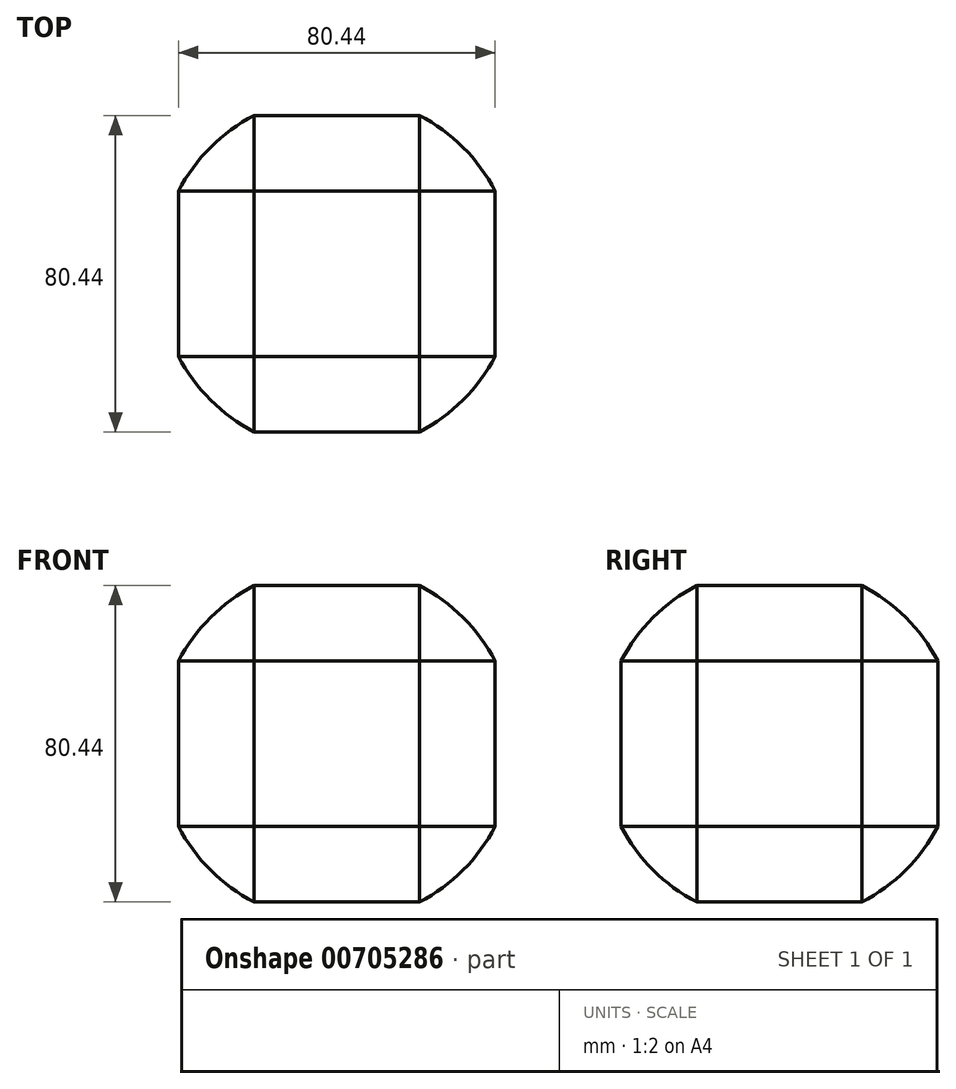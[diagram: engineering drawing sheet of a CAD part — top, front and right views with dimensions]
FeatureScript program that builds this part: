
annotation { "Feature Type Name" : "Feature", "Feature Type Description" : "" }
export const myFeature = defineFeature(function(context is Context, id is Id, definition is map)
    precondition{}
    {
        {
            var Q0;
            Q0=qCreatedBy(makeId("Top.planeOp"),FACE);
            var sketch = newSketch(context, id + "F0", { "sketchPlane" : qUnion([Q0])});
            skCircle(sketch, "E0", {"center": v(0, 0) * mm, "radius": 50 * mm});
            skLineSegment(sketch, "E1", {"start": v(0, 0) * mm, "end": v(69.26, 0) * mm, "construction": true});
            skLineSegment(sketch, "E2", {"start": v(0, 0) * mm, "end": v(-59.91, 0) * mm});
            skLineSegment(sketch, "E3", {"start": v(-59.91, 0) * mm, "end": v(73.8, 0) * mm});
            skSolve(sketch);
        }
        {
            var Q0;
            {var subQ0=sQuery(id+"F0.wireOp",EDGE,"E2");var subQ1=sQuery(id+"F0.wireOp",EDGE,"E0");var subQ2=makeQuery(id+"F0.imprint","INTERSECT",VERTEX,{"derivedFrom":[subQ1,subQ0]});Q0=makeQuery(id+"F0.imprint","IMPRINT",FACE,{"disambiguationData":[TD([[makeQuery(id+"F0.imprint","IMPRINT",EDGE,{"disambiguationData":[TD([[subQ2,1.0]])],"derivedFrom":subQ1}),1.0]])]});}
            var Q1;
            Q1=sQuery(id+"F0.wireOp",EDGE,"E3");
            revolve(context, id + "F1", {"surfaceOperationType" : NewSurfaceOperationType.NEW, "entities" : qUnion([Q0]), "axis" : qUnion([Q1]), "revolveType" : RevolveType.FULL});
        }
        {
            var Q0;
            Q0=qCreatedBy(makeId("Top.planeOp"),FACE);
            cPlane(context, id + "F2", {"entities" : qUnion([Q0]), "cplaneType" : CPlaneType.OFFSET, "offset" : 60 * mm, "width" : 150 * mm, "height" : 150 * mm});
        }
        {
            var Q0;
            Q0=qCreatedBy(id+"F2.planeOp",FACE);
            var sketch = newSketch(context, id + "F3", { "sketchPlane" : qUnion([Q0])});
            skCircle(sketch, "E4", {"center": v(0, 0) * mm, "radius": 45.37 * mm});
            skCircle(sketch, "E5", {"center": v(0, 0) * mm, "radius": 120.1 * mm});
            skSolve(sketch);
        }
        {
            var Q0;
            Q0=makeQuery(id+"F3.imprint","IMPRINT",FACE,{"disambiguationData":[TD([[makeQuery(id+"F3.imprint","IMPRINT",EDGE,{"derivedFrom":sQuery(id+"F3.wireOp",EDGE,"E4")}),-1.0]])]});
            extrude(context, id + "F4", {"entities" : qUnion([Q0]), "operationType" : NewBodyOperationType.REMOVE, "endBound" : BoundingType.THROUGH_ALL, "oppositeDirection" : true, "depth" : 25 * mm, "offsetDistance" : 25 * mm});
        }
        {
            var Q0;
            Q0=qCreatedBy(makeId("Front.planeOp"),FACE);
            cPlane(context, id + "F5", {"entities" : qUnion([Q0]), "cplaneType" : CPlaneType.OFFSET, "offset" : 60 * mm, "width" : 150 * mm, "height" : 150 * mm});
        }
        {
            var Q0;
            Q0=qCreatedBy(makeId("Right.planeOp"),FACE);
            cPlane(context, id + "F6", {"entities" : qUnion([Q0]), "cplaneType" : CPlaneType.OFFSET, "offset" : 60 * mm, "width" : 150 * mm, "height" : 150 * mm});
        }
        {
            var Q0;
            Q0=qCreatedBy(id+"F5.planeOp",FACE);
            var sketch = newSketch(context, id + "F7", { "sketchPlane" : qUnion([Q0])});
            skCircle(sketch, "E6", {"center": v(0, 0) * mm, "radius": 45.38 * mm});
            skCircle(sketch, "E7", {"center": v(0, 0) * mm, "radius": 63.17 * mm});
            skSolve(sketch);
        }
        {
            var Q0;
            Q0=makeQuery(id+"F7.imprint","IMPRINT",FACE,{"disambiguationData":[TD([[makeQuery(id+"F7.imprint","IMPRINT",EDGE,{"derivedFrom":sQuery(id+"F7.wireOp",EDGE,"E6")}),-1.0]])]});
            extrude(context, id + "F8", {"entities" : qUnion([Q0]), "operationType" : NewBodyOperationType.REMOVE, "endBound" : BoundingType.THROUGH_ALL, "oppositeDirection" : true, "depth" : 25 * mm, "offsetDistance" : 25 * mm});
        }
        {
            var Q0;
            Q0=qCreatedBy(id+"F6.planeOp",FACE);
            var sketch = newSketch(context, id + "F9", { "sketchPlane" : qUnion([Q0])});
            skCircle(sketch, "E8", {"center": v(0, 0) * mm, "radius": 45.38 * mm});
            skCircle(sketch, "E9", {"center": v(0, 0) * mm, "radius": 73.07 * mm});
            skSolve(sketch);
        }
        {
            var Q0;
            Q0=makeQuery(id+"F9.imprint","IMPRINT",FACE,{"disambiguationData":[TD([[makeQuery(id+"F9.imprint","IMPRINT",EDGE,{"derivedFrom":sQuery(id+"F9.wireOp",EDGE,"E8")}),-1.0]])]});
            extrude(context, id + "F10", {"entities" : qUnion([Q0]), "operationType" : NewBodyOperationType.REMOVE, "endBound" : BoundingType.THROUGH_ALL, "oppositeDirection" : true, "depth" : 25 * mm, "offsetDistance" : 25 * mm});
        }
        {
            var Q0;
            Q0=qCreatedBy(makeId("Right.planeOp"),FACE);
            var Q1;
            Q1=makeQuery(id+"F8.boolean.opBoolean","INTERSECT",VERTEX,{"disambiguationData":[OD(2.0)],"derivedFrom":[makeQuery(id+"F4.boolean.opBoolean","COPY",FACE,{"derivedFrom":makeQuery(id+"F4.opExtrude","SWEPT_FACE",FACE,{"disambiguationData":[OSD([sQuery(id+"F3.wireOp",EDGE,"E4")])]})}),makeQuery(id+"F4.boolean.opBoolean","SPLIT",FACE,{"disambiguationData":[OD(0.0)],"derivedFrom":makeQuery(id+"F1.opRevolve","SWEPT_FACE",FACE,{"disambiguationData":[OSD([sQuery(id+"F0.wireOp",EDGE,"E0")])]})}),makeQuery(id+"F8.opExtrude","SWEPT_FACE",FACE,{"disambiguationData":[OSD([sQuery(id+"F7.wireOp",EDGE,"E6")])]})]});
            cPlane(context, id + "F11", {"entities" : qUnion([Q0, Q1]), "cplaneType" : CPlaneType.PLANE_POINT, "offset" : 25 * mm, "width" : 150 * mm, "height" : 150 * mm});
        }
        {
            var Q0;
            Q0=qCreatedBy(id+"F11.planeOp",FACE);
            var sketch = newSketch(context, id + "F12", { "sketchPlane" : qUnion([Q0])});
            skLineSegment(sketch, "E10.bottom", {"start": v(-21, 21) * mm, "end": v(21, 21) * mm});
            skLineSegment(sketch, "E10.top", {"start": v(-21, -21) * mm, "end": v(21, -21) * mm});
            skLineSegment(sketch, "E10.left", {"start": v(-21, 21) * mm, "end": v(-21, -21) * mm});
            skLineSegment(sketch, "E10.right", {"start": v(21, 21) * mm, "end": v(21, -21) * mm});
            skSolve(sketch);
        }
        {
            var Q0;
            Q0=makeQuery(id+"F12.imprint","IMPRINT",FACE,{"disambiguationData":[TD([[makeQuery(id+"F12.imprint","IMPRINT",EDGE,{"derivedFrom":sQuery(id+"F12.wireOp",EDGE,"E10.bottom")}),-1.0]])]});
            extrude(context, id + "F13", {"entities" : qUnion([Q0]), "operationType" : NewBodyOperationType.REMOVE, "endBound" : BoundingType.THROUGH_ALL, "depth" : 25 * mm, "offsetDistance" : 25 * mm});
        }
        {
            var Q0;
            Q0=qCreatedBy(makeId("Right.planeOp"),FACE);
            var Q1;
            Q1=makeQuery(id+"F8.boolean.opBoolean","INTERSECT",VERTEX,{"disambiguationData":[OD(1.0)],"derivedFrom":[makeQuery(id+"F4.boolean.opBoolean","COPY",FACE,{"derivedFrom":makeQuery(id+"F4.opExtrude","SWEPT_FACE",FACE,{"disambiguationData":[OSD([sQuery(id+"F3.wireOp",EDGE,"E4")])]})}),makeQuery(id+"F4.boolean.opBoolean","SPLIT",FACE,{"disambiguationData":[OD(1.0)],"derivedFrom":makeQuery(id+"F1.opRevolve","SWEPT_FACE",FACE,{"disambiguationData":[OSD([sQuery(id+"F0.wireOp",EDGE,"E0")])]})}),makeQuery(id+"F8.opExtrude","SWEPT_FACE",FACE,{"disambiguationData":[OSD([sQuery(id+"F7.wireOp",EDGE,"E6")])]})]});
            cPlane(context, id + "F14", {"entities" : qUnion([Q0, Q1]), "cplaneType" : CPlaneType.PLANE_POINT, "offset" : 25 * mm, "width" : 150 * mm, "height" : 150 * mm});
        }
        {
            var Q0;
            Q0=qCreatedBy(id+"F14.planeOp",FACE);
            var sketch = newSketch(context, id + "F15", { "sketchPlane" : qUnion([Q0])});
            skLineSegment(sketch, "E11.bottom", {"start": v(21, 21) * mm, "end": v(-21, 21) * mm});
            skLineSegment(sketch, "E11.top", {"start": v(21, -21) * mm, "end": v(-21, -21) * mm});
            skLineSegment(sketch, "E11.left", {"start": v(21, 21) * mm, "end": v(21, -21) * mm});
            skLineSegment(sketch, "E11.right", {"start": v(-21, 21) * mm, "end": v(-21, -21) * mm});
            skSolve(sketch);
        }
        {
            var Q0;
            Q0=makeQuery(id+"F15.imprint","IMPRINT",FACE,{"disambiguationData":[TD([[makeQuery(id+"F15.imprint","IMPRINT",EDGE,{"derivedFrom":sQuery(id+"F15.wireOp",EDGE,"E11.bottom")}),1.0]])]});
            extrude(context, id + "F16", {"entities" : qUnion([Q0]), "operationType" : NewBodyOperationType.REMOVE, "endBound" : BoundingType.THROUGH_ALL, "oppositeDirection" : true, "depth" : 25 * mm, "offsetDistance" : 25 * mm});
        }
        {
            var Q0;
            Q0=qCreatedBy(makeId("Top.planeOp"),FACE);
            var Q1;
            Q1=makeQuery(id+"F10.boolean.opBoolean","INTERSECT",VERTEX,{"disambiguationData":[OD(1.0)],"derivedFrom":[makeQuery(id+"F8.boolean.opBoolean","SPLIT",FACE,{"disambiguationData":[OD(1.0)],"derivedFrom":makeQuery(id+"F4.boolean.opBoolean","SPLIT",FACE,{"disambiguationData":[OD(1.0)],"derivedFrom":makeQuery(id+"F1.opRevolve","SWEPT_FACE",FACE,{"disambiguationData":[OSD([sQuery(id+"F0.wireOp",EDGE,"E0")])]})})}),makeQuery(id+"F8.boolean.opBoolean","COPY",FACE,{"disambiguationData":[OD(1.0)],"derivedFrom":makeQuery(id+"F8.opExtrude","SWEPT_FACE",FACE,{"disambiguationData":[OSD([sQuery(id+"F7.wireOp",EDGE,"E6")])]})}),makeQuery(id+"F10.opExtrude","SWEPT_FACE",FACE,{"disambiguationData":[OSD([sQuery(id+"F9.wireOp",EDGE,"E8")])]})]});
            cPlane(context, id + "F17", {"entities" : qUnion([Q0, Q1]), "cplaneType" : CPlaneType.PLANE_POINT, "offset" : 25 * mm, "width" : 150 * mm, "height" : 150 * mm});
        }
        {
            var Q0;
            Q0=qCreatedBy(id+"F17.planeOp",FACE);
            var sketch = newSketch(context, id + "F18", { "sketchPlane" : qUnion([Q0])});
            skLineSegment(sketch, "E12.bottom", {"start": v(-21, 21) * mm, "end": v(21, 21) * mm});
            skLineSegment(sketch, "E12.top", {"start": v(-21, -21) * mm, "end": v(21, -21) * mm});
            skLineSegment(sketch, "E12.left", {"start": v(-21, 21) * mm, "end": v(-21, -21) * mm});
            skLineSegment(sketch, "E12.right", {"start": v(21, 21) * mm, "end": v(21, -21) * mm});
            skSolve(sketch);
        }
        {
            var Q0;
            Q0=makeQuery(id+"F18.imprint","IMPRINT",FACE,{"disambiguationData":[TD([[makeQuery(id+"F18.imprint","IMPRINT",EDGE,{"derivedFrom":sQuery(id+"F18.wireOp",EDGE,"E12.bottom")}),-1.0]])]});
            extrude(context, id + "F19", {"entities" : qUnion([Q0]), "operationType" : NewBodyOperationType.REMOVE, "endBound" : BoundingType.THROUGH_ALL, "depth" : 25 * mm, "offsetDistance" : 25 * mm});
        }
        {
            var Q0;
            Q0=qCreatedBy(makeId("Front.planeOp"),FACE);
            var sketch = newSketch(context, id + "F20", { "sketchPlane" : qUnion([Q0])});
            skLineSegment(sketch, "E13.bottom", {"start": v(21, -58.86) * mm, "end": v(-21, -58.86) * mm});
            skLineSegment(sketch, "E13.top", {"start": v(21, -40.22) * mm, "end": v(-21, -40.22) * mm});
            skLineSegment(sketch, "E13.left", {"start": v(21, -58.86) * mm, "end": v(21, -40.22) * mm});
            skLineSegment(sketch, "E13.right", {"start": v(-21, -58.86) * mm, "end": v(-21, -40.22) * mm});
            skSolve(sketch);
        }
        {
            var Q0;
            Q0 = qSketchRegion(id + "F20", true);
            extrude(context, id + "F21", {"entities" : qUnion([Q0]), "operationType" : NewBodyOperationType.REMOVE, "endBound" : BoundingType.THROUGH_ALL, "oppositeDirection" : true, "depth" : 25 * mm, "offsetDistance" : 25 * mm, "hasSecondDirection" : true, "secondDirectionBound" : SecondDirectionBoundingType.THROUGH_ALL, "secondDirectionOppositeDirection" : false, "secondDirectionDepth" : 25 * mm});
        }
        {
            var Q0;
            Q0=qCreatedBy(makeId("Right.planeOp"),FACE);
            var sketch = newSketch(context, id + "F22", { "sketchPlane" : qUnion([Q0])});
            skLineSegment(sketch, "E14.bottom", {"start": v(-53.94, 21) * mm, "end": v(-40.22, 21) * mm});
            skLineSegment(sketch, "E14.top", {"start": v(-53.94, -21) * mm, "end": v(-40.22, -21) * mm});
            skLineSegment(sketch, "E14.left", {"start": v(-53.94, 21) * mm, "end": v(-53.94, -21) * mm});
            skLineSegment(sketch, "E14.right", {"start": v(-40.22, 21) * mm, "end": v(-40.22, -21) * mm});
            skLineSegment(sketch, "E15.bottom", {"start": v(64.02, 21) * mm, "end": v(40.22, 21) * mm});
            skLineSegment(sketch, "E15.top", {"start": v(64.02, -21) * mm, "end": v(40.22, -21) * mm});
            skLineSegment(sketch, "E15.left", {"start": v(64.02, 21) * mm, "end": v(64.02, -21) * mm});
            skLineSegment(sketch, "E15.right", {"start": v(40.22, 21) * mm, "end": v(40.22, -21) * mm});
            skSolve(sketch);
        }
        {
            var Q0;
            Q0 = qSketchRegion(id + "F22", true);
            extrude(context, id + "F23", {"entities" : qUnion([Q0]), "operationType" : NewBodyOperationType.REMOVE, "endBound" : BoundingType.THROUGH_ALL, "oppositeDirection" : true, "depth" : 25 * mm, "offsetDistance" : 25 * mm, "hasSecondDirection" : true, "secondDirectionBound" : SecondDirectionBoundingType.THROUGH_ALL, "secondDirectionOppositeDirection" : false, "secondDirectionDepth" : 25 * mm});
        }
    });
